# Revit family: Kosz_na_smieci_z_pokrywa_wiszacy_30 l
name_source: partatom
category: Furniture
units: mm (PartAtom-declared; Revit-internal decimal feet)

## family parameters
Always vertical = Yes
Cut with Voids When Loaded = No
Host = Wall
Room Calculation Point = No
Shared = No

## types (1)
- WB30S
    Depth / Glebokosc = 214 mm  [stored 0.7021 ft]
    Description = Kosz na śmieci o pojemności 30 l montowany jest na ścianie. Posiada uchylną pokrywę, zasłaniającą wnętrze kubła, co zapewnia wysoki poziom higieny. To prosty w obsłudze i czyszczeniu, uniwersalny pojemnik na śmieci, który bez problemu można wkomponować w różnorodne wnętrza toalet publicznych. Dzięki użytej do produkcji stali nierdzewnej model ten jest bardzo wytrzymały i odporny na wszelkie akty wandalizmu. Stalowy kosz naścienny o dużej pojemności sprawdza się we wszystkich toaletach publicznych.
    Height / Wysokosc = 625 mm  [stored 2.05052 ft]
    Manufacturer = FANECO.com
    Manufacturer code / Kod producenta = 5901764292142
    Material = Stal nierdzewna szczotkowana
    Material finish / Wykonczenie = Stal nierdzewna 430 szczotkowana
    Product code / Kod produktu = WB30S
    Type Comments = Kosz na śmieci z pokrywą wiszący 30 l stal szlachetna matowa
    URL = https://faneco.com
    Weight / Waga = 5 kg
    Width / Szerokosc = 304 mm  [stored 0.997375 ft]

note: [stored X ft] marks values corroborated as IEEE doubles in the binary element streams (Revit-internal decimal feet)

## geometry (parser evidence)
native form markers: Sweep x8
no freeform markers — native parametric forms only
